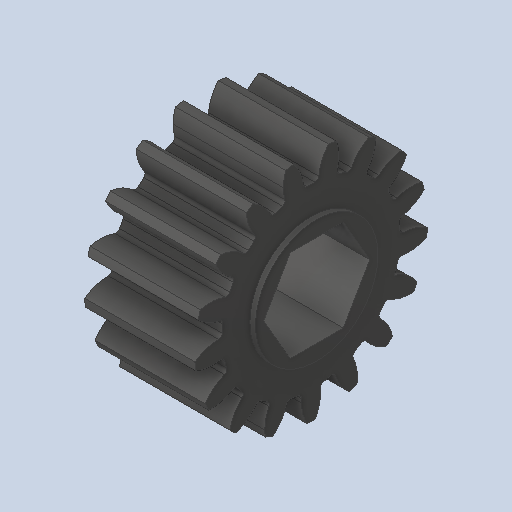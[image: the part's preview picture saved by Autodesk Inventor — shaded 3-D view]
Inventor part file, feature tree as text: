
AUTODESK INVENTOR PART (.ipt)
format: ipt  version: 2023.4 (Build 274418000, 418)  size: 274,944 bytes
history: native  units: in
note: dims shown in document units (in); Inventor stores cm internally (conversion verified against a paired STEP export)
features: fillet x1
ambient origin geometry x8: Origin, YZ Plane, XZ Plane, XY Plane, X Axis, Y Axis, Z Axis, Center Point
bodies: Solid1 (feature_tree)
feature tree (1):
  fillet  "Fillet1"  [1 undecoded]
note: 1 required parameter value undecoded (feature->parameter linkage not recoverable at this tier; creation-order binding heuristic only, values carry confidence <= 0.55)
